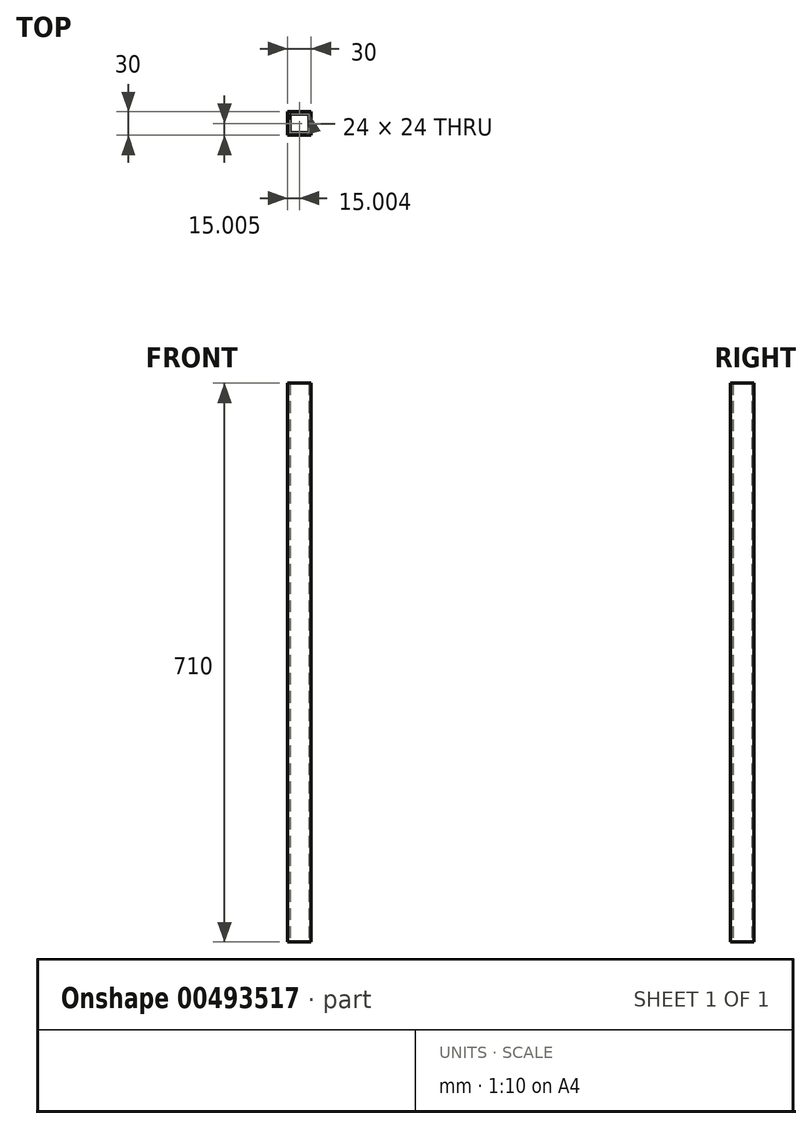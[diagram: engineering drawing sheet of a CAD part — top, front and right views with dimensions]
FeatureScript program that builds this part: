
annotation { "Feature Type Name" : "Feature", "Feature Type Description" : "" }
export const myFeature = defineFeature(function(context is Context, id is Id, definition is map)
    precondition{}
    {
        {
            var Q0;
            Q0=qCreatedBy(makeId("Top.planeOp"),FACE);
            var sketch = newSketch(context, id + "F0", { "sketchPlane" : qUnion([Q0])});
            skLineSegment(sketch, "E0.bottom", {"start": v(-9.77, 6.43) * mm, "end": v(14.23, 6.43) * mm});
            skLineSegment(sketch, "E0.top", {"start": v(-9.77, -17.57) * mm, "end": v(14.23, -17.57) * mm});
            skLineSegment(sketch, "E0.left", {"start": v(-9.77, 6.43) * mm, "end": v(-9.77, -17.57) * mm});
            skLineSegment(sketch, "E0.right", {"start": v(14.23, 6.43) * mm, "end": v(14.23, -17.57) * mm});
            skLineSegment(sketch, "E1.bottom", {"start": v(-12.77, 9.43) * mm, "end": v(17.23, 9.43) * mm});
            skLineSegment(sketch, "E1.top", {"start": v(-12.77, -20.57) * mm, "end": v(17.23, -20.57) * mm});
            skLineSegment(sketch, "E1.left", {"start": v(-12.77, 9.43) * mm, "end": v(-12.77, -20.57) * mm});
            skLineSegment(sketch, "E1.right", {"start": v(17.23, 9.43) * mm, "end": v(17.23, -20.57) * mm});
            skSolve(sketch);
        }
        {
            var Q0;
            Q0=qSketchRegion(id+"F0",true);
            extrude(context, id + "F1", {"entities" : qUnion([Q0]), "depth" : 710 * mm});
        }
    });
